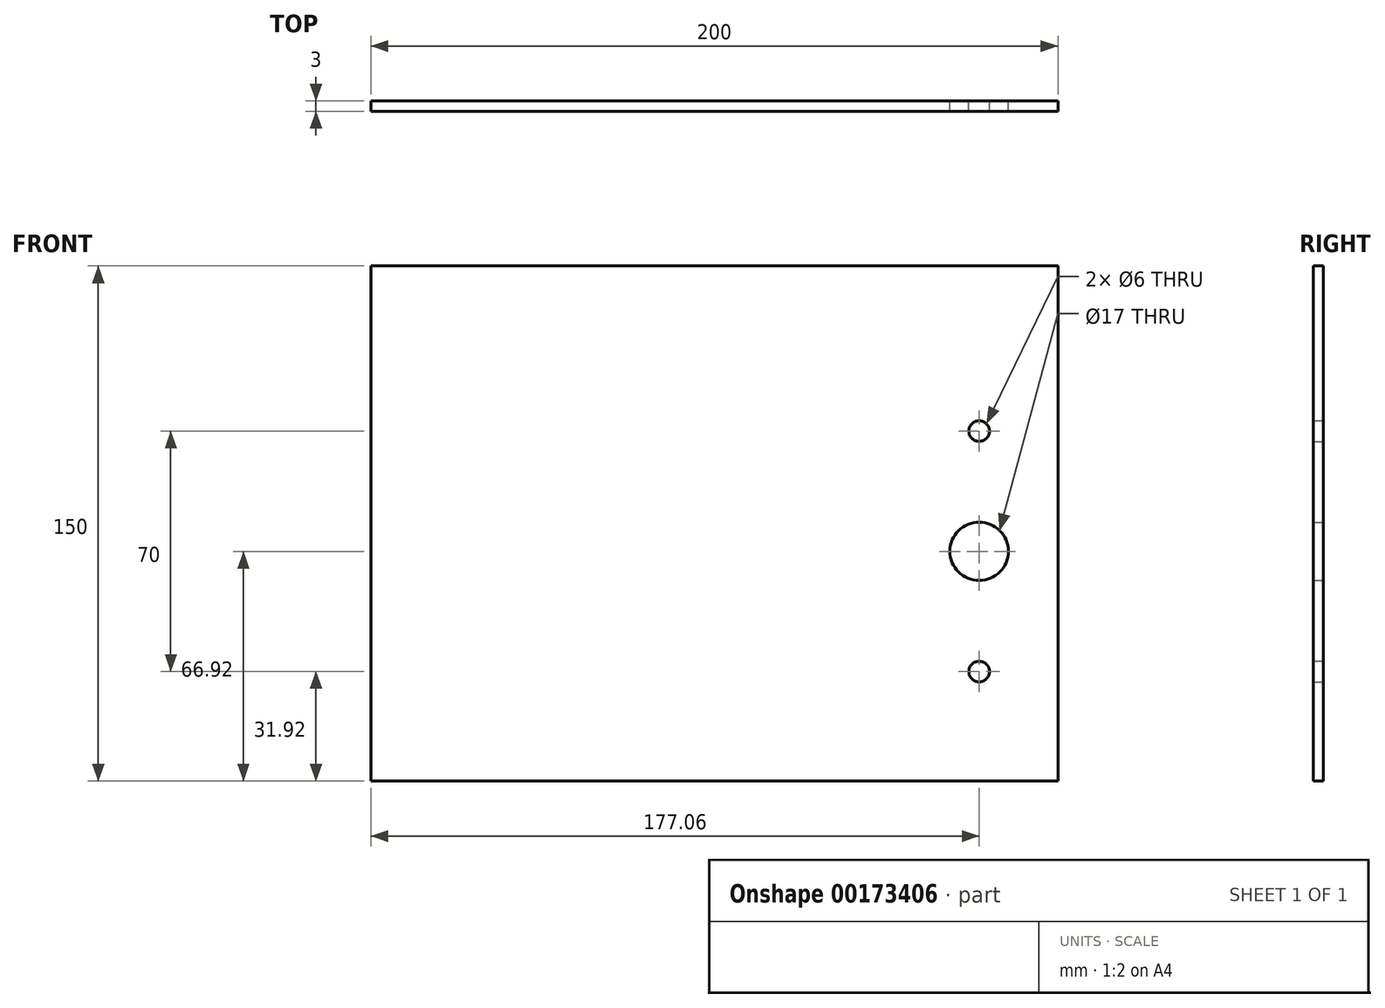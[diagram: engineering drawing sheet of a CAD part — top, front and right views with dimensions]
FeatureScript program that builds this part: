
annotation { "Feature Type Name" : "Feature", "Feature Type Description" : "" }
export const myFeature = defineFeature(function(context is Context, id is Id, definition is map)
    precondition{}
    {
        {
            var Q0;
            Q0=qCreatedBy(makeId("Front.planeOp"),FACE);
            var sketch = newSketch(context, id + "F0", { "sketchPlane" : qUnion([Q0])});
            skLineSegment(sketch, "E0.bottom", {"start": v(-107.06, 83.08) * mm, "end": v(92.94, 83.08) * mm});
            skLineSegment(sketch, "E0.top", {"start": v(-107.06, -66.92) * mm, "end": v(92.94, -66.92) * mm});
            skLineSegment(sketch, "E0.left", {"start": v(-107.06, 83.08) * mm, "end": v(-107.06, -66.92) * mm});
            skLineSegment(sketch, "E0.right", {"start": v(92.94, 83.08) * mm, "end": v(92.94, -66.92) * mm});
            skCircle(sketch, "E1", {"center": v(70, 0) * mm, "radius": 8.5 * mm});
            skCircle(sketch, "E2", {"center": v(70, 35) * mm, "radius": 3 * mm});
            skCircle(sketch, "E3.MirrorC", {"center": v(70, -35) * mm, "radius": 3 * mm});
            skSolve(sketch);
        }
        {
            var Q0;
            Q0 = qSketchRegion(id + "F0", true);
            extrude(context, id + "F1", {"entities" : qUnion([Q0]), "depth" : 3 * mm});
        }
    });
